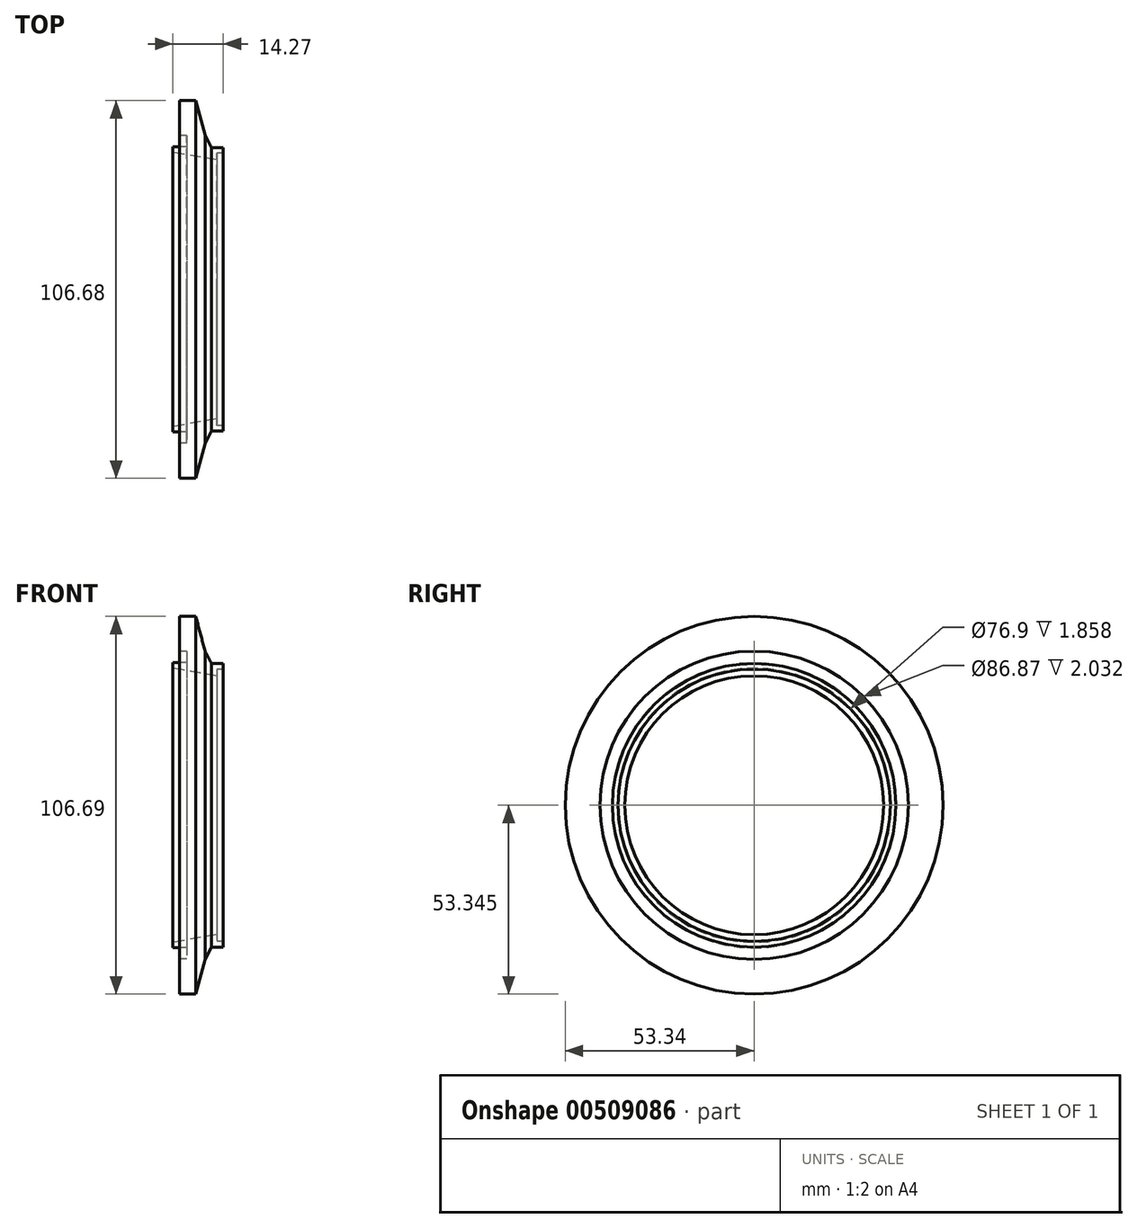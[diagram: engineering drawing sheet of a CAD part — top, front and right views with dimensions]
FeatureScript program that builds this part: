
annotation { "Feature Type Name" : "Feature", "Feature Type Description" : "" }
export const myFeature = defineFeature(function(context is Context, id is Id, definition is map)
    precondition{}
    {
        {
            var Q0;
            Q0=qCreatedBy(makeId("Front.planeOp"),FACE);
            var sketch = newSketch(context, id + "F0", { "sketchPlane" : qUnion([Q0])});
            skLineSegment(sketch, "E0", {"start": v(0, 0) * mm, "end": v(0, 1.52) * mm});
            skLineSegment(sketch, "E1", {"start": v(0, 1.52) * mm, "end": v(3.96, 1.52) * mm});
            skLineSegment(sketch, "E2", {"start": v(3.96, 1.52) * mm, "end": v(3.96, 4.7) * mm});
            skLineSegment(sketch, "E3", {"start": v(3.96, 4.7) * mm, "end": v(1.93, 4.7) * mm});
            skLineSegment(sketch, "E4", {"start": v(1.93, 4.7) * mm, "end": v(1.93, 14.6) * mm});
            skLineSegment(sketch, "E5", {"start": v(1.93, 14.6) * mm, "end": v(6.5, 14.6) * mm});
            skLineSegment(sketch, "E6", {"start": v(6.5, 14.6) * mm, "end": v(9.13, 4.8) * mm});
            skPoint(sketch, "E7.orphan", {"position": v(14.27, 0.65) * mm});
            skLineSegment(sketch, "E8", {"start": v(0, -38.74) * mm, "end": v(14.27, -38.74) * mm});
            skLineSegment(sketch, "E9", {"start": v(0, 0) * mm, "end": v(12.42, -2.19) * mm});
            skPoint(sketch, "E10.end.orphan", {"position": v(12.42, 0.65) * mm});
            skLineSegment(sketch, "E11", {"start": v(12.42, -0.28) * mm, "end": v(12.42, -2.19) * mm});
            skPoint(sketch, "E12.start.orphan", {"position": v(14.27, -1.57) * mm});
            skLineSegment(sketch, "E13", {"start": v(12.42, -0.28) * mm, "end": v(14.27, -0.28) * mm});
            skLineSegment(sketch, "E14", {"start": v(14.27, -0.28) * mm, "end": v(14.27, 1.3) * mm});
            skLineSegment(sketch, "E15", {"start": v(9.13, 4.8) * mm, "end": v(10.98, 1.3) * mm});
            skLineSegment(sketch, "E16", {"start": v(10.98, 1.3) * mm, "end": v(14.27, 1.3) * mm});
            skSolve(sketch);
        }
        {
            var Q0;
            Q0=makeQuery(id+"F0.imprint","IMPRINT",FACE,{"disambiguationData":[TD([[makeQuery(id+"F0.imprint","IMPRINT",EDGE,{"derivedFrom":sQuery(id+"F0.wireOp",EDGE,"E0")}),-1.0]])]});
            var Q1;
            Q1=sQuery(id+"F0.wireOp",EDGE,"E8");
            revolve(context, id + "F1", {"entities" : qUnion([Q0]), "axis" : qUnion([Q1]), "revolveType" : RevolveType.FULL});
        }
    });
